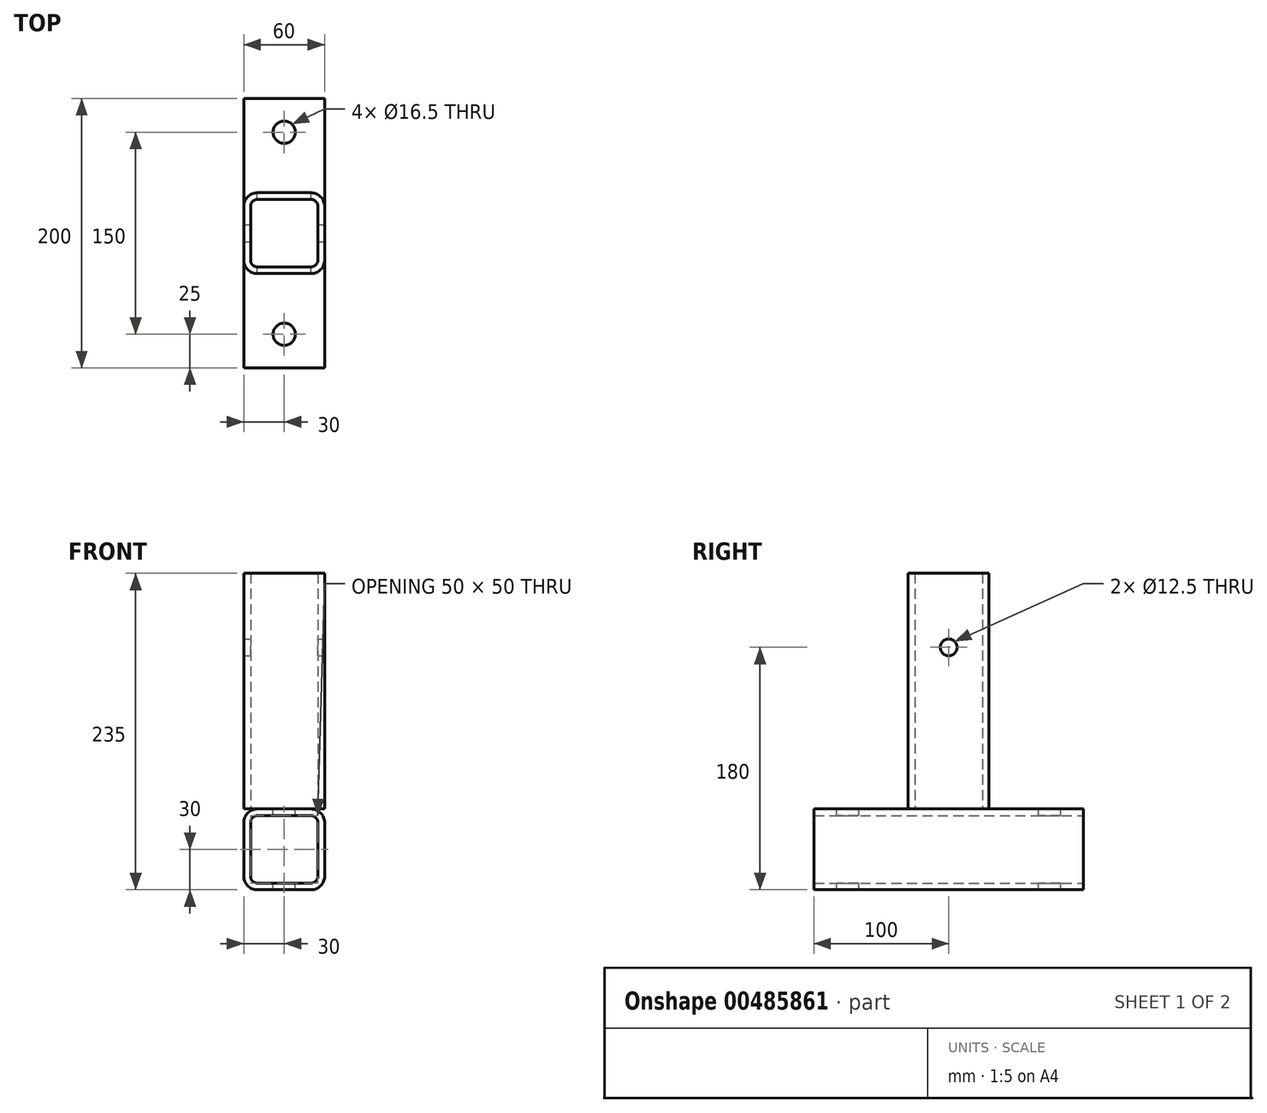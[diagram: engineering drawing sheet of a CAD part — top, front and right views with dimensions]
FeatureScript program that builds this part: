
annotation { "Feature Type Name" : "Feature", "Feature Type Description" : "" }
export const myFeature = defineFeature(function(context is Context, id is Id, definition is map)
    precondition{}
    {
        {
            var Q0;
            Q0=qCreatedBy(makeId("Top.planeOp"),FACE);
            var sketch = newSketch(context, id + "F0", { "sketchPlane" : qUnion([Q0])});
            skLineSegment(sketch, "E0.bottom", {"start": v(-20, 30) * mm, "end": v(20, 30) * mm});
            skLineSegment(sketch, "E0.top", {"start": v(-20, -30) * mm, "end": v(20, -30) * mm});
            skLineSegment(sketch, "E0.left", {"start": v(-30, 20) * mm, "end": v(-30, -20) * mm});
            skLineSegment(sketch, "E0.right", {"start": v(30, 20) * mm, "end": v(30, -20) * mm});
            skPoint(sketch, "E0.middle", {"position": v(0, 0) * mm});
            skPoint(sketch, "E1.visualSharp", {"position": v(-30, -30) * mm});
            skArc(sketch, "E1.filletArc", {"start": v(-30, -20) * mm, "mid": v(-27.07, -27.07) * mm, "end": v(-20, -30) * mm});
            skPoint(sketch, "E2.visualSharp", {"position": v(30, -30) * mm});
            skArc(sketch, "E2.filletArc", {"start": v(20, -30) * mm, "mid": v(27.07, -27.07) * mm, "end": v(30, -20) * mm});
            skPoint(sketch, "E3.visualSharp", {"position": v(30, 30) * mm});
            skArc(sketch, "E3.filletArc", {"start": v(30, 20) * mm, "mid": v(27.07, 27.07) * mm, "end": v(20, 30) * mm});
            skPoint(sketch, "E4.visualSharp", {"position": v(-30, 30) * mm});
            skArc(sketch, "E4.filletArc", {"start": v(-20, 30) * mm, "mid": v(-27.07, 27.07) * mm, "end": v(-30, 20) * mm});
            skArc(sketch, "E5.0", {"start": v(-20, 25) * mm, "mid": v(-23.54, 23.54) * mm, "end": v(-25, 20) * mm});
            skLineSegment(sketch, "E5.1", {"start": v(-20, 25) * mm, "end": v(20, 25) * mm});
            skLineSegment(sketch, "E5.2", {"start": v(-25, 20) * mm, "end": v(-25, -20) * mm});
            skArc(sketch, "E5.3", {"start": v(25, 20) * mm, "mid": v(23.54, 23.54) * mm, "end": v(20, 25) * mm});
            skArc(sketch, "E5.4", {"start": v(-25, -20) * mm, "mid": v(-23.54, -23.54) * mm, "end": v(-20, -25) * mm});
            skLineSegment(sketch, "E5.5", {"start": v(-20, -25) * mm, "end": v(20, -25) * mm});
            skArc(sketch, "E5.6", {"start": v(20, -25) * mm, "mid": v(23.54, -23.54) * mm, "end": v(25, -20) * mm});
            skLineSegment(sketch, "E5.7", {"start": v(25, 20) * mm, "end": v(25, -20) * mm});
            skSolve(sketch);
        }
        {
            var Q0;
            Q0 = qSketchRegion(id + "F0", true);
            extrude(context, id + "F1", {"entities" : qUnion([Q0]), "endBound" : BoundingType.SYMMETRIC, "depth" : 175 * mm, "offsetDistance" : 25 * mm});
        }
        {
            var Q0;
            Q0=qCreatedBy(makeId("Front.planeOp"),FACE);
            var sketch = newSketch(context, id + "F2", { "sketchPlane" : qUnion([Q0])});
            skLineSegment(sketch, "E6.bottom", {"start": v(-20, -87.5) * mm, "end": v(20, -87.5) * mm});
            skLineSegment(sketch, "E6.top", {"start": v(-20, -147.5) * mm, "end": v(20, -147.5) * mm});
            skLineSegment(sketch, "E6.left", {"start": v(-30, -97.5) * mm, "end": v(-30, -137.5) * mm});
            skLineSegment(sketch, "E6.right", {"start": v(30, -97.5) * mm, "end": v(30, -137.5) * mm});
            skPoint(sketch, "E6.middle", {"position": v(0, -117.5) * mm});
            skPoint(sketch, "E7.visualSharp", {"position": v(30, -87.5) * mm});
            skArc(sketch, "E7.filletArc", {"start": v(30, -97.5) * mm, "mid": v(27.07, -90.43) * mm, "end": v(20, -87.5) * mm});
            skPoint(sketch, "E8.visualSharp", {"position": v(-30, -87.5) * mm});
            skArc(sketch, "E8.filletArc", {"start": v(-20, -87.5) * mm, "mid": v(-27.07, -90.43) * mm, "end": v(-30, -97.5) * mm});
            skPoint(sketch, "E9.visualSharp", {"position": v(-30, -147.5) * mm});
            skArc(sketch, "E9.filletArc", {"start": v(-30, -137.5) * mm, "mid": v(-27.07, -144.57) * mm, "end": v(-20, -147.5) * mm});
            skPoint(sketch, "E10.visualSharp", {"position": v(30, -147.5) * mm});
            skArc(sketch, "E10.filletArc", {"start": v(20, -147.5) * mm, "mid": v(27.07, -144.57) * mm, "end": v(30, -137.5) * mm});
            skLineSegment(sketch, "E11.0", {"start": v(25, -97.5) * mm, "end": v(25, -137.5) * mm});
            skArc(sketch, "E11.1", {"start": v(20, -142.5) * mm, "mid": v(23.54, -141.04) * mm, "end": v(25, -137.5) * mm});
            skArc(sketch, "E11.2", {"start": v(25, -97.5) * mm, "mid": v(23.54, -93.96) * mm, "end": v(20, -92.5) * mm});
            skLineSegment(sketch, "E11.3", {"start": v(-20, -142.5) * mm, "end": v(20, -142.5) * mm});
            skLineSegment(sketch, "E11.4", {"start": v(-20, -92.5) * mm, "end": v(20, -92.5) * mm});
            skArc(sketch, "E11.5", {"start": v(-20, -92.5) * mm, "mid": v(-23.54, -93.96) * mm, "end": v(-25, -97.5) * mm});
            skLineSegment(sketch, "E11.6", {"start": v(-25, -97.5) * mm, "end": v(-25, -137.5) * mm});
            skArc(sketch, "E11.7", {"start": v(-25, -137.5) * mm, "mid": v(-23.54, -141.04) * mm, "end": v(-20, -142.5) * mm});
            skSolve(sketch);
        }
        {
            var Q0;
            Q0 = qSketchRegion(id + "F2", true);
            extrude(context, id + "F3", {"entities" : qUnion([Q0]), "operationType" : NewBodyOperationType.ADD, "endBound" : BoundingType.SYMMETRIC, "depth" : 200 * mm, "offsetDistance" : 25 * mm});
        }
        {
            var Q0;
            {var subQ3=sQuery(id+"F0.wireOp",EDGE,"E0.bottom");var subQ5=sQuery(id+"F2.wireOp",EDGE,"E6.bottom");Q0=makeQuery(id+"F3.boolean.opBoolean","SPLIT",FACE,{"disambiguationData":[TD([makeQuery(id+"F1.opExtrude","SWEPT_FACE",FACE,{"disambiguationData":[OSD([subQ3])]})])],"derivedFrom":makeQuery(id+"F3.opExtrude","SWEPT_FACE",FACE,{"disambiguationData":[OSD([subQ5])]})});}
            var sketch = newSketch(context, id + "F4", { "sketchPlane" : qUnion([Q0])});
            skCircle(sketch, "E12", {"center": v(0, 75) * mm, "radius": 8.25 * mm});
            skLineSegment(sketch, "E13", {"start": v(0, 0) * mm, "end": v(-89.08, 0) * mm, "construction": true});
            skCircle(sketch, "E14.MirrorC", {"center": v(0, -75) * mm, "radius": 8.25 * mm});
            skSolve(sketch);
        }
        {
            var Q0;
            Q0 = qSketchRegion(id + "F4", true);
            extrude(context, id + "F5", {"entities" : qUnion([Q0]), "operationType" : NewBodyOperationType.REMOVE, "endBound" : BoundingType.THROUGH_ALL, "oppositeDirection" : true, "depth" : 25 * mm, "offsetDistance" : 25 * mm});
        }
        {
            var Q0;
            Q0=makeQuery(id+"F1.opExtrude","SWEPT_FACE",FACE,{"disambiguationData":[OSD([sQuery(id+"F0.wireOp",EDGE,"E0.right")])]});
            var sketch = newSketch(context, id + "F6", { "sketchPlane" : qUnion([Q0])});
            skCircle(sketch, "E15", {"center": v(0, 32.5) * mm, "radius": 6.25 * mm});
            skSolve(sketch);
        }
        {
            var Q0;
            Q0 = qSketchRegion(id + "F6", true);
            extrude(context, id + "F7", {"entities" : qUnion([Q0]), "operationType" : NewBodyOperationType.REMOVE, "endBound" : BoundingType.THROUGH_ALL, "oppositeDirection" : true, "depth" : 25 * mm, "offsetDistance" : 25 * mm});
        }
    });
